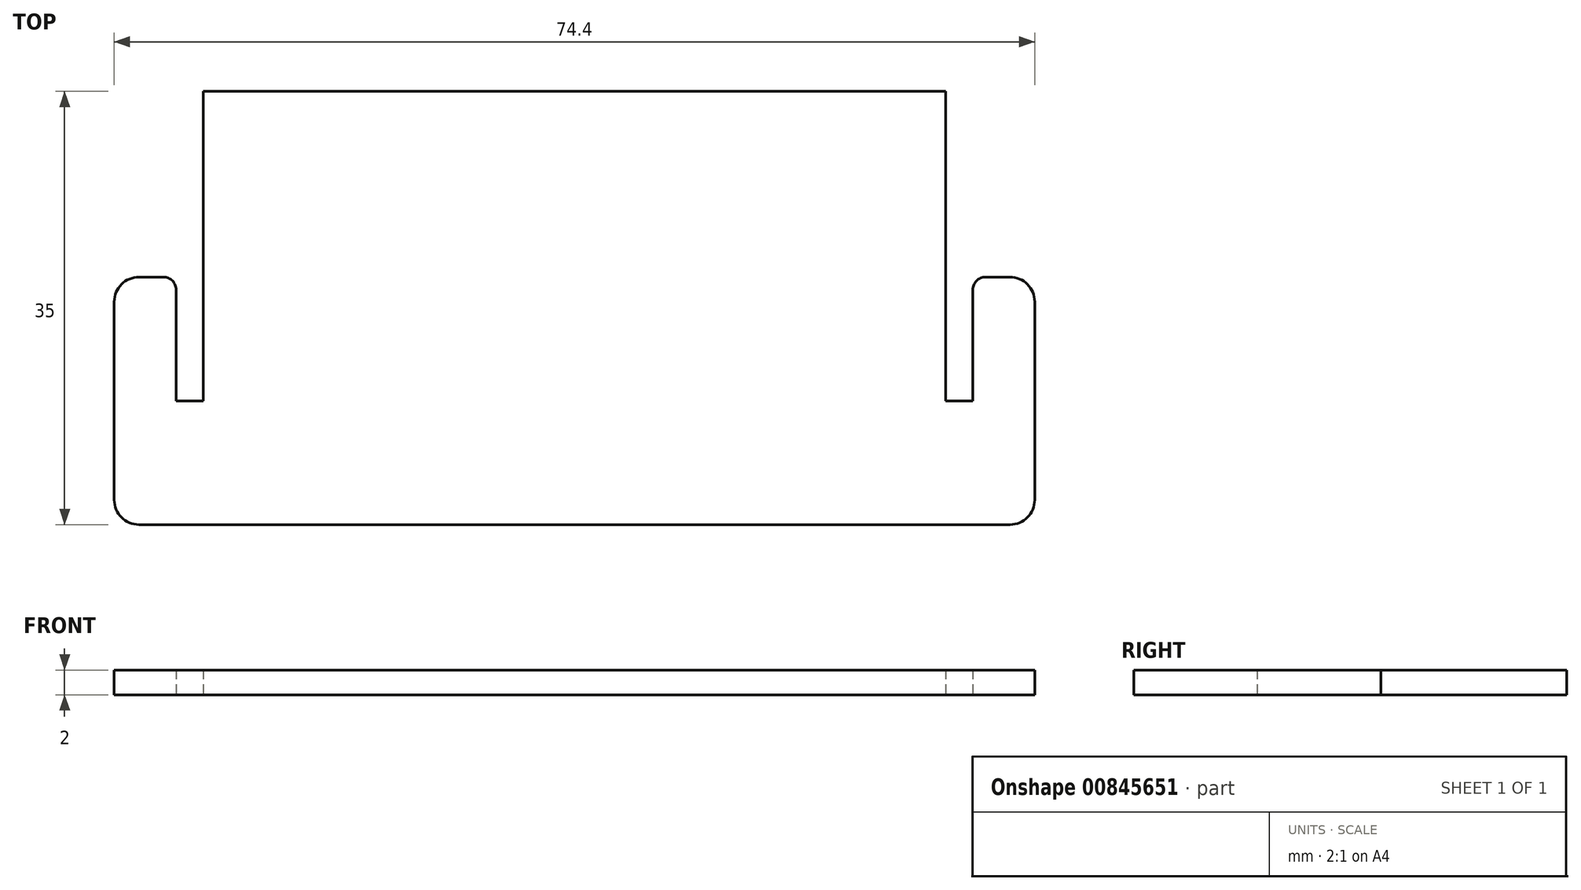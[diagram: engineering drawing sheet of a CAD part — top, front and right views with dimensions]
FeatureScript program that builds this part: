
annotation { "Feature Type Name" : "Feature", "Feature Type Description" : "" }
export const myFeature = defineFeature(function(context is Context, id is Id, definition is map)
    precondition{}
    {
        {
            var Q0;
            Q0=qCreatedBy(makeId("Top.planeOp"),FACE);
            var sketch = newSketch(context, id + "F0", { "sketchPlane" : qUnion([Q0])});
            skLineSegment(sketch, "E0", {"start": v(-21.84, 12.46) * mm, "end": v(71.3, 12.46) * mm, "construction": true});
            skLineSegment(sketch, "E1", {"start": v(-22.55, -22.54) * mm, "end": v(84.96, -22.54) * mm, "construction": true});
            skLineSegment(sketch, "E2", {"start": v(-12.16, 34.3) * mm, "end": v(-12.16, -35.5) * mm, "construction": true});
            skLineSegment(sketch, "E3", {"start": v(47.84, 32.9) * mm, "end": v(47.84, -41.22) * mm, "construction": true});
            skLineSegment(sketch, "E4", {"start": v(-12.16, 12.46) * mm, "end": v(47.84, 12.46) * mm});
            skLineSegment(sketch, "E5", {"start": v(47.84, 12.46) * mm, "end": v(47.84, -22.54) * mm});
            skLineSegment(sketch, "E6", {"start": v(47.84, -22.54) * mm, "end": v(-12.16, -22.54) * mm});
            skLineSegment(sketch, "E7", {"start": v(-12.16, -22.54) * mm, "end": v(-12.16, 12.46) * mm});
            skLineSegment(sketch, "E8.MirrorCS", {"start": v(47.84, -22.54) * mm, "end": v(50.04, -22.54) * mm});
            skLineSegment(sketch, "E9.MirrorCS", {"start": v(50.04, -22.54) * mm, "end": v(53.04, -22.54) * mm});
            skArc(sketch, "E10.MirrorCS", {"start": v(50.04, -3.57) * mm, "mid": v(50.34, -2.84) * mm, "end": v(51.07, -2.54) * mm});
            skLineSegment(sketch, "E11.MirrorCS", {"start": v(50.04, -12.54) * mm, "end": v(47.84, -12.54) * mm});
            skLineSegment(sketch, "E12.MirrorCS", {"start": v(53.04, -2.54) * mm, "end": v(51.07, -2.54) * mm});
            skArc(sketch, "E13.MirrorCS", {"start": v(55.04, -20.54) * mm, "mid": v(54.46, -21.96) * mm, "end": v(53.04, -22.54) * mm});
            skArc(sketch, "E14.MirrorCS", {"start": v(53.04, -2.54) * mm, "mid": v(54.46, -3.13) * mm, "end": v(55.04, -4.54) * mm});
            skLineSegment(sketch, "E15.MirrorCS", {"start": v(47.84, -12.54) * mm, "end": v(47.84, -22.54) * mm});
            skLineSegment(sketch, "E16.MirrorCS", {"start": v(55.04, -20.54) * mm, "end": v(55.04, -4.54) * mm});
            skLineSegment(sketch, "E17.MirrorCS", {"start": v(50.04, -3.57) * mm, "end": v(50.04, -12.54) * mm});
            skLineSegment(sketch, "E18", {"start": v(17.84, 18.8) * mm, "end": v(17.84, -45.43) * mm, "construction": true});
            skLineSegment(sketch, "E19.MirrorCS", {"start": v(-17.36, -2.54) * mm, "end": v(-15.38, -2.54) * mm});
            skArc(sketch, "E20.MirrorCS", {"start": v(-14.36, -3.57) * mm, "mid": v(-14.66, -2.84) * mm, "end": v(-15.38, -2.54) * mm});
            skLineSegment(sketch, "E21.MirrorCS", {"start": v(-12.16, -22.54) * mm, "end": v(-14.36, -22.54) * mm});
            skLineSegment(sketch, "E22.MirrorCS", {"start": v(-14.36, -12.54) * mm, "end": v(-12.16, -12.54) * mm});
            skLineSegment(sketch, "E23.MirrorCS", {"start": v(-14.36, -22.54) * mm, "end": v(-17.36, -22.54) * mm});
            skLineSegment(sketch, "E24.MirrorCS", {"start": v(-19.36, -20.54) * mm, "end": v(-19.36, -4.54) * mm});
            skLineSegment(sketch, "E25.MirrorCS", {"start": v(-14.36, -3.57) * mm, "end": v(-14.36, -12.54) * mm});
            skLineSegment(sketch, "E26.MirrorCS", {"start": v(-12.16, -12.54) * mm, "end": v(-12.16, -22.54) * mm});
            skArc(sketch, "E27.MirrorCS", {"start": v(-19.36, -20.54) * mm, "mid": v(-18.77, -21.96) * mm, "end": v(-17.36, -22.54) * mm});
            skArc(sketch, "E28.MirrorCS", {"start": v(-17.36, -2.54) * mm, "mid": v(-18.77, -3.13) * mm, "end": v(-19.36, -4.54) * mm});
            skSolve(sketch);
        }
        {
            var Q0;
            {var subQ1=sQuery(id+"F0.wireOp",EDGE,"E8.MirrorCS");var subQ6=sQuery(id+"F0.wireOp",EDGE,"E4");Q0=qUnion([makeQuery(id+"F0.imprint","IMPRINT",FACE,{"disambiguationData":[TD([[makeQuery(id+"F0.imprint","IMPRINT",EDGE,{"derivedFrom":subQ1}),1.0]])]}),makeQuery(id+"F0.imprint","IMPRINT",FACE,{"disambiguationData":[TD([[makeQuery(id+"F0.imprint","IMPRINT",EDGE,{"derivedFrom":sQuery(id+"F0.wireOp",EDGE,"E19.MirrorCS")}),-1.0]])]}),makeQuery(id+"F0.imprint","IMPRINT",FACE,{"disambiguationData":[TD([[makeQuery(id+"F0.imprint","IMPRINT",EDGE,{"derivedFrom":subQ6}),-1.0]])]})]);}
            extrude(context, id + "F1", {"entities" : qUnion([Q0]), "depth" : 2 * mm, "offsetDistance" : 25 * mm});
        }
    });
